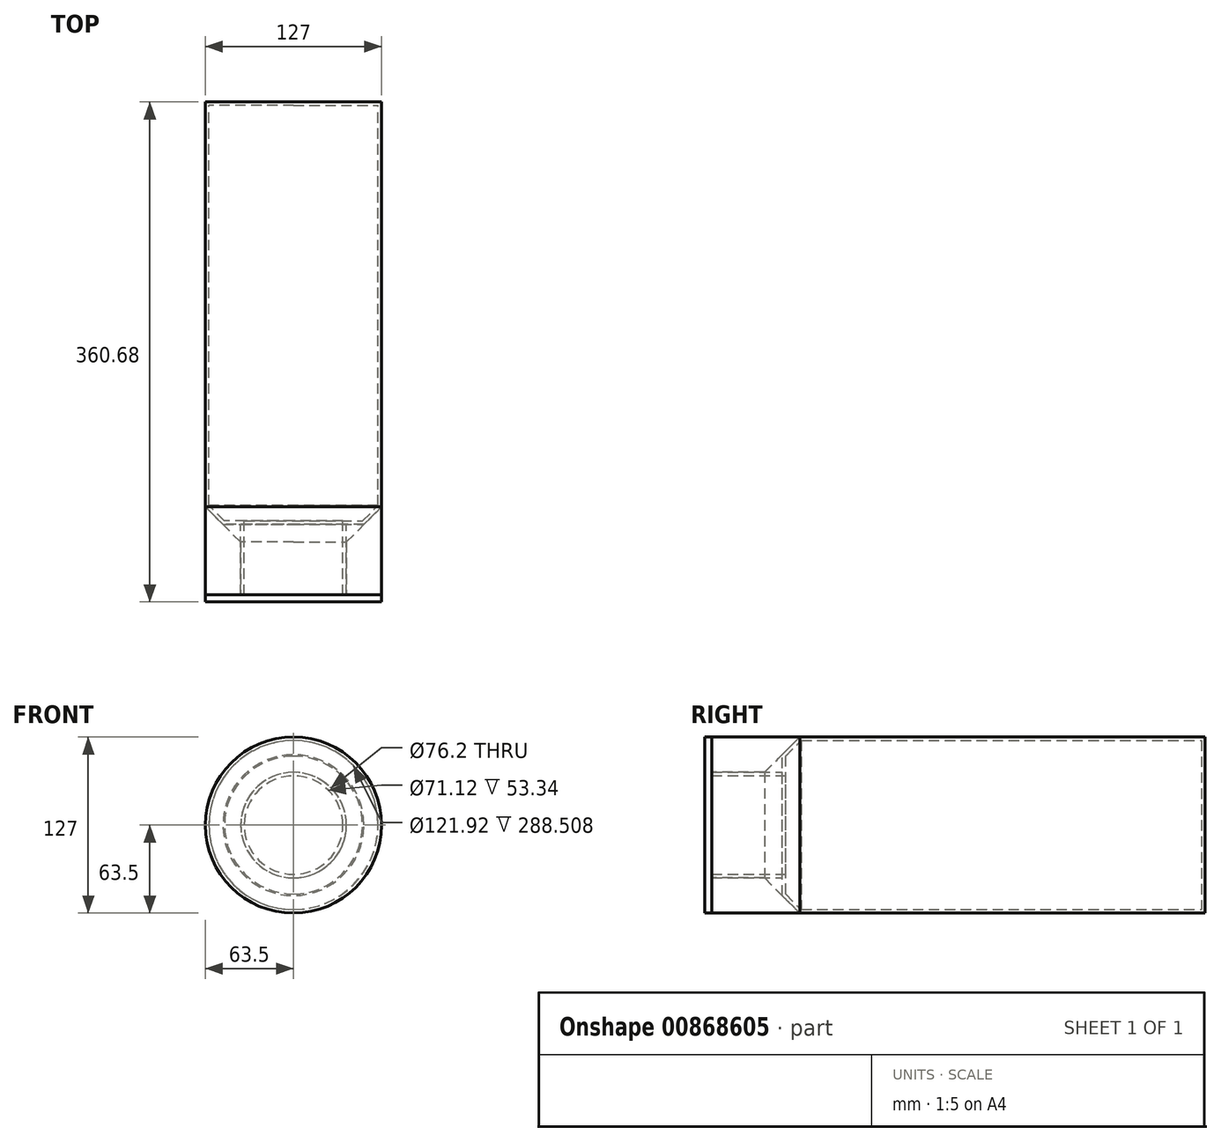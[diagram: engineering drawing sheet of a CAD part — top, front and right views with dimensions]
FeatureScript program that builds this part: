
annotation { "Feature Type Name" : "Feature", "Feature Type Description" : "" }
export const myFeature = defineFeature(function(context is Context, id is Id, definition is map)
    precondition{}
    {
        {
            var Q0;
            Q0=qCreatedBy(makeId("Front.planeOp"),FACE);
            var sketch = newSketch(context, id + "F0", { "sketchPlane" : qUnion([Q0])});
            skCircle(sketch, "E0", {"center": v(0, 0) * mm, "radius": 63.5 * mm});
            skCircle(sketch, "E1", {"center": v(0, 0) * mm, "radius": 38.1 * mm});
            skSolve(sketch);
        }
        {
            var Q0;
            Q0=makeQuery(id+"F0.imprint","IMPRINT",FACE,{"disambiguationData":[TD([[makeQuery(id+"F0.imprint","IMPRINT",EDGE,{"derivedFrom":sQuery(id+"F0.wireOp",EDGE,"E1")}),1.0]])]});
            extrude(context, id + "F1", {"entities" : qUnion([Q0]), "depth" : 355.6 * mm, "offsetDistance" : 25.4 * mm});
        }
        {
            var Q0;
            Q0 = qSketchRegion(id + "F0", true);
            extrude(context, id + "F2", {"entities" : qUnion([Q0]), "operationType" : NewBodyOperationType.ADD, "depth" : 304.8 * mm, "offsetDistance" : 25.4 * mm});
        }
        {
            var Q0;
            Q0=makeQuery(id+"F2.opExtrude","CAP_EDGE",EDGE,{"disambiguationData":[OSD([sQuery(id+"F0.wireOp",EDGE,"E0")])],"isStart":false});
            chamfer(context, id + "F3", {"entities" : qUnion([Q0]), "width" : 12.7 * mm, "tangentPropagation" : true});
        }
        {
            var Q0;
            Q0=makeQuery(id+"F1.opExtrude","CAP_FACE",FACE,{"disambiguationData":[OSD([sQuery(id+"F0.wireOp",EDGE,"E1")])],"isStart":false});
            shell(context, id + "F4", {"entities" : qUnion([Q0]), "thickness" : 2.54 * mm});
        }
        {
            var Q0;
            Q0=makeQuery(id+"F1.opExtrude","CAP_FACE",FACE,{"disambiguationData":[OSD([sQuery(id+"F0.wireOp",EDGE,"E1")])],"isStart":false});
            var sketch = newSketch(context, id + "F5", { "sketchPlane" : qUnion([Q0])});
            skCircle(sketch, "E2.0", {"center": v(0, 0) * mm, "radius": 63.5 * mm});
            skCircle(sketch, "E3.0", {"center": v(0, 0) * mm, "radius": 38.1 * mm});
            skSolve(sketch);
        }
        {
            var Q0;
            Q0=makeQuery(id+"F5.imprint","IMPRINT",FACE,{"disambiguationData":[TD([[makeQuery(id+"F5.imprint","IMPRINT",EDGE,{"derivedFrom":sQuery(id+"F5.wireOp",EDGE,"E2.0")}),1.0]])]});
            var Q1;
            Q1=makeQuery(id+"F3.opChamfer","BLEND_FACE",FACE,{"disambiguationData":[OSD([sQuery(id+"F0.wireOp",EDGE,"E0")])]});
            extrude(context, id + "F6", {"entities" : qUnion([Q0]), "endBound" : BoundingType.UP_TO_SURFACE, "oppositeDirection" : true, "depth" : 25.4 * mm, "endBoundEntityFace" : qUnion([Q1]), "offsetDistance" : 25.4 * mm});
        }
        {
            var Q0;
            Q0=makeQuery(id+"F5.imprint","IMPRINT",FACE,{"disambiguationData":[TD([[makeQuery(id+"F5.imprint","IMPRINT",EDGE,{"derivedFrom":sQuery(id+"F5.wireOp",EDGE,"E2.0")}),1.0]])]});
            var Q1;
            Q1=makeQuery(id+"F5.imprint","IMPRINT",FACE,{"disambiguationData":[TD([[makeQuery(id+"F5.imprint","IMPRINT",EDGE,{"derivedFrom":makeQuery(id+"F4.opShell","OFFSET_EDGE",EDGE,{"disambiguationData":[OSD([sQuery(id+"F0.wireOp",EDGE,"E1")])]})}),1.0]])]});
            var Q2;
            Q2=makeQuery(id+"F5.imprint","IMPRINT",FACE,{"disambiguationData":[TD([[makeQuery(id+"F5.imprint","IMPRINT",EDGE,{"derivedFrom":sQuery(id+"F5.wireOp",EDGE,"E3.0")}),1.0]])]});
            extrude(context, id + "F7", {"entities" : qUnion([Q0, Q1, Q2]), "depth" : 5.08 * mm, "offsetDistance" : 25.4 * mm});
        }
    });
